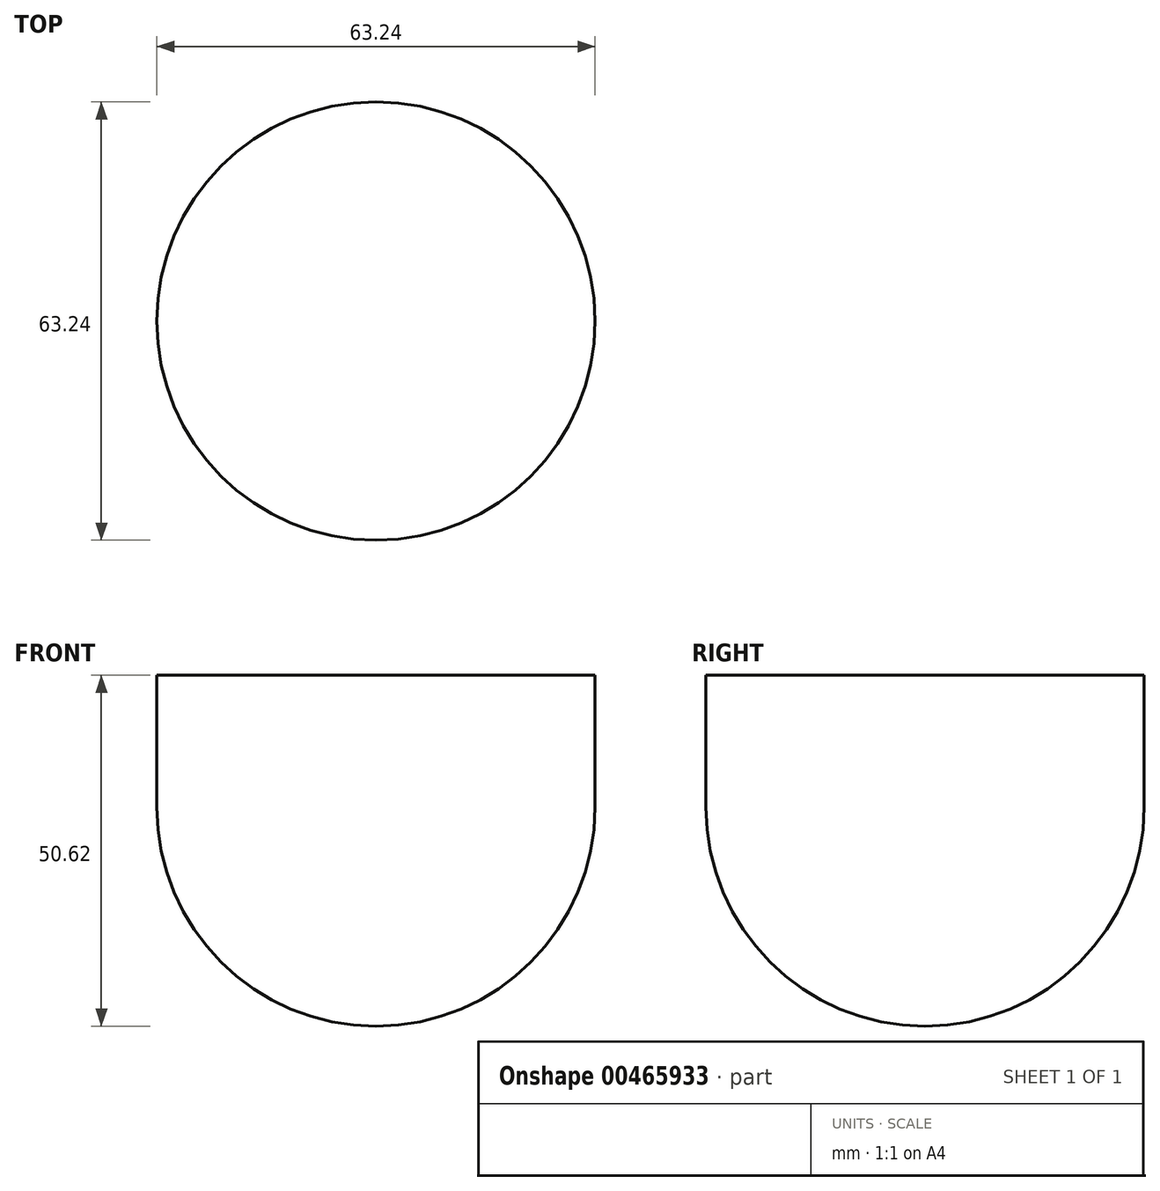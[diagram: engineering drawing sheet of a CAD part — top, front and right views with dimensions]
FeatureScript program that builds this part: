
annotation { "Feature Type Name" : "Feature", "Feature Type Description" : "" }
export const myFeature = defineFeature(function(context is Context, id is Id, definition is map)
    precondition{}
    {
        {
            var Q0;
            Q0=qCreatedBy(makeId("Top.planeOp"),FACE);
            var sketch = newSketch(context, id + "F0", { "sketchPlane" : qUnion([Q0])});
            skCircle(sketch, "E0", {"center": v(0, 0) * mm, "radius": 31.62 * mm});
            skLineSegment(sketch, "E1", {"start": v(0, 31.62) * mm, "end": v(0, -31.62) * mm});
            skSolve(sketch);
        }
        {
            var Q0;
            {var subQ0=sQuery(id+"F0.wireOp",EDGE,"E1");Q0=makeQuery(id+"F0.imprint","IMPRINT",FACE,{"disambiguationData":[TD([[makeQuery(id+"F0.imprint","IMPRINT",EDGE,{"derivedFrom":subQ0}),-1.0]])]});}
            var Q1;
            Q1=sQuery(id+"F0.wireOp",EDGE,"E1");
            revolve(context, id + "F1", {"entities" : qUnion([Q0]), "axis" : qUnion([Q1]), "revolveType" : RevolveType.ONE_DIRECTION, "angle" : 180 * degree});
        }
        {
            var Q0;
            {var subQ0=sQuery(id+"F0.wireOp",EDGE,"E1");Q0=makeQuery(id+"F0.imprint","IMPRINT",FACE,{"disambiguationData":[TD([[makeQuery(id+"F0.imprint","IMPRINT",EDGE,{"derivedFrom":subQ0}),-1.0]])]});}
            var Q1;
            {var subQ0=sQuery(id+"F0.wireOp",EDGE,"E1");Q1=makeQuery(id+"F0.imprint","IMPRINT",FACE,{"disambiguationData":[TD([[makeQuery(id+"F0.imprint","IMPRINT",EDGE,{"derivedFrom":subQ0}),1.0]])]});}
            extrude(context, id + "F2", {"entities" : qUnion([Q0, Q1]), "operationType" : NewBodyOperationType.ADD, "depth" : 19 * mm});
        }
    });
